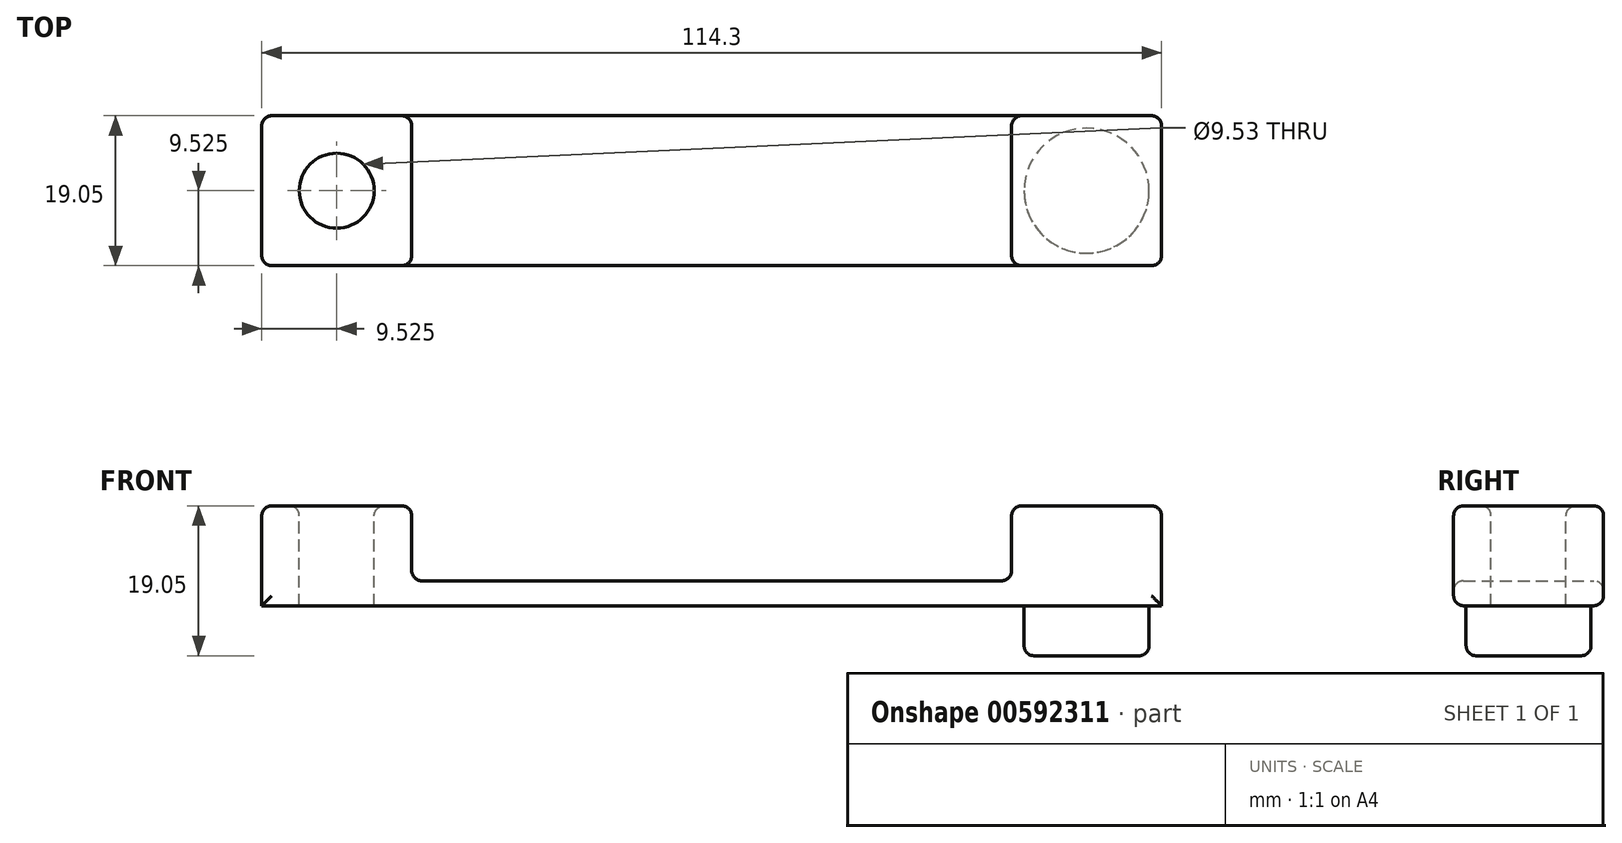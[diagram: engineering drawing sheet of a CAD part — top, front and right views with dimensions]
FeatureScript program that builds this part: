
annotation { "Feature Type Name" : "Feature", "Feature Type Description" : "" }
export const myFeature = defineFeature(function(context is Context, id is Id, definition is map)
    precondition{}
    {
        {
            var Q0;
            Q0=qCreatedBy(makeId("Front.planeOp"),FACE);
            var sketch = newSketch(context, id + "F0", { "sketchPlane" : qUnion([Q0])});
            skLineSegment(sketch, "E0", {"start": v(-57.15, 0) * mm, "end": v(0, 0) * mm});
            skLineSegment(sketch, "E1", {"start": v(0, 0) * mm, "end": v(57.15, 0) * mm});
            skLineSegment(sketch, "E2", {"start": v(57.15, 0) * mm, "end": v(57.15, 19.05) * mm});
            skLineSegment(sketch, "E3", {"start": v(57.15, 19.05) * mm, "end": v(38.1, 19.05) * mm});
            skLineSegment(sketch, "E4", {"start": v(38.1, 19.05) * mm, "end": v(38.1, 9.53) * mm});
            skLineSegment(sketch, "E5", {"start": v(38.1, 9.53) * mm, "end": v(-38.1, 9.53) * mm});
            skLineSegment(sketch, "E6", {"start": v(-38.1, 9.53) * mm, "end": v(-38.1, 19.05) * mm});
            skLineSegment(sketch, "E7", {"start": v(-38.1, 19.05) * mm, "end": v(-57.15, 19.05) * mm});
            skLineSegment(sketch, "E8", {"start": v(-57.15, 19.05) * mm, "end": v(-57.15, 0) * mm});
            skSolve(sketch);
        }
        {
            var Q0;
            Q0=makeQuery(id+"F0.imprint","IMPRINT",FACE,{"disambiguationData":[TD([[makeQuery(id+"F0.imprint","IMPRINT",EDGE,{"derivedFrom":sQuery(id+"F0.wireOp",EDGE,"E0")}),1.0]])]});
            extrude(context, id + "F1", {"entities" : qUnion([Q0]), "depth" : 19.05 * mm, "offsetDistance" : 25.4 * mm});
        }
        {
            var Q0;
            Q0=makeQuery(id+"F1.opExtrude","SWEPT_FACE",FACE,{"disambiguationData":[OSD([sQuery(id+"F0.wireOp",EDGE,"E7")])]});
            var sketch = newSketch(context, id + "F2", { "sketchPlane" : qUnion([Q0])});
            skPoint(sketch, "E9.endSnap0", {"position": v(-47.62, 0) * mm});
            skCircle(sketch, "E10", {"center": v(-47.62, -9.53) * mm, "radius": 4.76 * mm});
            skCircle(sketch, "E11.MirrorC", {"center": v(47.62, -9.53) * mm, "radius": 4.76 * mm});
            skLineSegment(sketch, "E12", {"start": v(-57.15, 0) * mm, "end": v(-47.62, -9.53) * mm, "construction": true});
            skLineSegment(sketch, "E13", {"start": v(-47.62, -9.53) * mm, "end": v(-38.1, -19.05) * mm, "construction": true});
            skSolve(sketch);
        }
        {
            var Q0;
            Q0=makeQuery(id+"F2.imprint","IMPRINT",FACE,{"disambiguationData":[TD([[makeQuery(id+"F2.imprint","IMPRINT",EDGE,{"derivedFrom":sQuery(id+"F2.wireOp",EDGE,"E10")}),1.0]])]});
            var Q1;
            Q1=makeQuery(id+"F2.imprint","IMPRINT",FACE,{"disambiguationData":[TD([[makeQuery(id+"F2.imprint","IMPRINT",EDGE,{"derivedFrom":sQuery(id+"F2.wireOp",EDGE,"E11.MirrorC")}),-1.0]])]});
            extrude(context, id + "F3", {"entities" : qUnion([Q0, Q1]), "operationType" : NewBodyOperationType.REMOVE, "endBound" : BoundingType.THROUGH_ALL, "oppositeDirection" : true, "depth" : 25.4 * mm, "offsetDistance" : 25.4 * mm});
        }
        {
            var Q0;
            Q0=makeQuery(id+"F1.opExtrude","SWEPT_FACE",FACE,{"disambiguationData":[OSD([sQuery(id+"F0.wireOp",EDGE,"E0"),sQuery(id+"F0.wireOp",EDGE,"E1")])]});
            var sketch = newSketch(context, id + "F4", { "sketchPlane" : qUnion([Q0])});
            skCircle(sketch, "E14", {"center": v(-47.62, 9.53) * mm, "radius": 7.94 * mm});
            skCircle(sketch, "E15.MirrorC", {"center": v(47.62, 9.53) * mm, "radius": 7.94 * mm});
            skSolve(sketch);
        }
        {
            var Q0;
            Q0=makeQuery(id+"F4.imprint","IMPRINT",FACE,{"disambiguationData":[TD([[makeQuery(id+"F4.imprint","IMPRINT",EDGE,{"derivedFrom":sQuery(id+"F4.wireOp",EDGE,"E14")}),1.0]])]});
            var Q1;
            Q1=makeQuery(id+"F4.imprint","IMPRINT",FACE,{"disambiguationData":[TD([[makeQuery(id+"F4.imprint","IMPRINT",EDGE,{"derivedFrom":sQuery(id+"F4.wireOp",EDGE,"E15.MirrorC")}),-1.0]])]});
            extrude(context, id + "F5", {"entities" : qUnion([Q0, Q1]), "operationType" : NewBodyOperationType.REMOVE, "oppositeDirection" : true, "depth" : 6.35 * mm, "offsetDistance" : 25.4 * mm});
        }
        {
            var Q0;
            Q0=makeQuery(id+"F1.opExtrude","CAP_FACE",FACE,{"disambiguationData":[OSD([sQuery(id+"F0.wireOp",EDGE,"E0"),sQuery(id+"F0.wireOp",EDGE,"E1"),sQuery(id+"F0.wireOp",EDGE,"E2"),sQuery(id+"F0.wireOp",EDGE,"E3"),sQuery(id+"F0.wireOp",EDGE,"E4"),sQuery(id+"F0.wireOp",EDGE,"E5"),sQuery(id+"F0.wireOp",EDGE,"E6"),sQuery(id+"F0.wireOp",EDGE,"E7"),sQuery(id+"F0.wireOp",EDGE,"E8")])],"isStart":false});
            var Q1;
            Q1=makeQuery(id+"F1.opExtrude","CAP_FACE",FACE,{"disambiguationData":[OSD([sQuery(id+"F0.wireOp",EDGE,"E0"),sQuery(id+"F0.wireOp",EDGE,"E1"),sQuery(id+"F0.wireOp",EDGE,"E2"),sQuery(id+"F0.wireOp",EDGE,"E3"),sQuery(id+"F0.wireOp",EDGE,"E4"),sQuery(id+"F0.wireOp",EDGE,"E5"),sQuery(id+"F0.wireOp",EDGE,"E6"),sQuery(id+"F0.wireOp",EDGE,"E7"),sQuery(id+"F0.wireOp",EDGE,"E8")])],"isStart":true});
            var Q2;
            Q2=makeQuery(id+"F1.opExtrude","SWEPT_FACE",FACE,{"disambiguationData":[OSD([sQuery(id+"F0.wireOp",EDGE,"E5")])]});
            var Q3;
            Q3=makeQuery(id+"F1.opExtrude","SWEPT_FACE",FACE,{"disambiguationData":[OSD([sQuery(id+"F0.wireOp",EDGE,"E3")])]});
            var Q4;
            Q4=makeQuery(id+"F1.opExtrude","SWEPT_FACE",FACE,{"disambiguationData":[OSD([sQuery(id+"F0.wireOp",EDGE,"E7")])]});
            var Q5;
            Q5=makeQuery(id+"F1.opExtrude","SWEPT_FACE",FACE,{"disambiguationData":[OSD([sQuery(id+"F0.wireOp",EDGE,"E0"),sQuery(id+"F0.wireOp",EDGE,"E1")])]});
            fillet(context, id + "F6", {"entities" : qUnion([Q0, Q1, Q2, Q3, Q4, Q5]), "radius" : 1.27 * mm, "tangentPropagation" : true, "allowEdgeOverflow" : false});
        }
    });
